# Revit family: Haworth_JiveTable_RacetrackLegs
name_source: partatom
category: Furniture Systems
revit_build: Autodesk Revit 2018 (Build: 20170223_1515(x64)
units: mm (PartAtom-declared; Revit-internal decimal feet)

## family parameters
Always vertical = Yes
Cut with Voids When Loaded = No
OmniClass Number = 23.40.70.14.64.21
OmniClass Title = Systems Furniture
Part Type = Normal
Room Calculation Point = No
Round Connector Dimension = Use Diameter
Shared = No
Work Plane-Based = No

## types (46) — shared parameters
Assembly Code = E2020200
Custom Size = No
Manufacturer = Haworth, Inc.
Max. Depth = 48"
Max. Height = 29"
Max. Width = 96"
Min. Depth = 30"
Min. Height = 16"
Min. Width = 48"
Model = Hawoth Jive
Revision Number = 0
Size = Verify Final Dim. w/ Haworth
Standard Depths = 30, 36, 42, 48 in.
Standard Height = 16, 20. 29 in.
Standard Widths = 48, 60, 72, 84, 96 in.
Table Thickness = 1 3/16"
URL = https://www.haworth.com
URL - Product = http://www.haworth.com
Warranty = http://www.haworth.com

## per-type parameters (varying)
| type | Actual Casters | Actual Depth | Actual Height | Actual Width | Casters | Depth | Description | Glides | Height | Leg Distance | Leg Height | Leg Length | Leg Spacing | Post Extruded Base | Post Round Base | T Leg Extruded | Table Radius | Width |
| 30d 48w 16h - Post Extruded Base - With Glides | No | 30" | 16" | 48" | No | 30" | Haworth Jive Table Racetrack Legs - 30d 48w 16h - Post Extruded Base - With Glides | Yes | 16" | 11 1/2" | 14 13/16" | 11" | 8" | Yes | No | No | 15" | 48" |
| 30d 60w 16h - Post Extruded Base - With Glides | No | 30" | 16" | 60" | No | 30" | Haworth Jive Table Racetrack Legs - 30d 60w 16h - Post Extruded Base - With Glides | Yes | 16" | 11 1/2" | 14 13/16" | 11" | 8" | Yes | No | No | 15" | 60" |
| 30d 72w 16h - Post Extruded Base - With Glides | No | 30" | 16" | 72" | No | 30" | Haworth Jive Table Racetrack Legs - 30d 72w 16h - Post Extruded Base - With Glides | Yes | 16" | 11 1/2" | 14 13/16" | 11" | 8" | Yes | No | No | 15" | 72" |
| 36d 60w 16h - Post Extruded Base - With Glides | No | 36" | 16" | 60" | No | 36" | Haworth Jive Table Racetrack Legs - 36d 60w 16h - Post Extruded Base - With Glides | Yes | 16" | 11 1/2" | 14 13/16" | 11" | 11" | Yes | No | No | 18" | 60" |
| 36d 72w 16h - Post Extruded Base - With Glides | No | 36" | 16" | 72" | No | 36" | Haworth Jive Table Racetrack Legs - 36d 72w 16h - Post Extruded Base - With Glides | Yes | 16" | 11 1/2" | 14 13/16" | 11" | 11" | Yes | No | No | 18" | 72" |
| 36d 84w 16h - Post Extruded Base - With Glides | No | 36" | 16" | 84" | No | 36" | Haworth Jive Table Racetrack Legs - 36d 84w 16h - Post Extruded Base - With Glides | Yes | 16" | 11 1/2" | 14 13/16" | 11" | 11" | Yes | No | No | 18" | 84" |
| 30d 48w 20h - Post Extruded Base - With Glides | No | 30" | 20" | 48" | No | 30" | Haworth Jive Table Racetrack Legs - 30d 48w 20h - Post Extruded Base - With Glides | Yes | 20" | 11 1/2" | 18 13/16" | 11" | 8" | Yes | No | No | 15" | 48" |
| 30d 60w 20h - Post Extruded Base - With Glides | No | 30" | 20" | 60" | No | 30" | Haworth Jive Table Racetrack Legs - 30d 60w 20h - Post Extruded Base - With Glides | Yes | 20" | 11 1/2" | 18 13/16" | 11" | 8" | Yes | No | No | 15" | 60" |
| 30d 72w 20h - Post Extruded Base - With Glides | No | 30" | 20" | 72" | No | 30" | Haworth Jive Table Racetrack Legs - 30d 72w 20h - Post Extruded Base - With Glides | Yes | 20" | 11 1/2" | 18 13/16" | 11" | 8" | Yes | No | No | 15" | 72" |
| 36d 60w 20h - Post Extruded Base - With Glides | No | 36" | 20" | 60" | No | 36" | Haworth Jive Table Racetrack Legs - 36d 60w 20h - Post Extruded Base - With Glides | Yes | 20" | 11 1/2" | 18 13/16" | 11" | 11" | Yes | No | No | 18" | 60" |
| 36d 72w 20h - Post Extruded Base - With Glides | No | 36" | 20" | 72" | No | 36" | Haworth Jive Table Racetrack Legs - 36d 72w 20h - Post Extruded Base - With Glides | Yes | 20" | 11 1/2" | 18 13/16" | 11" | 11" | Yes | No | No | 18" | 72" |
| 36d 84w 20h - Post Extruded Base - With Glides | No | 36" | 20" | 84" | No | 36" | Haworth Jive Table Racetrack Legs - 36d 84w 20h - Post Extruded Base - With Glides | Yes | 20" | 11 1/2" | 18 13/16" | 11" | 11" | Yes | No | No | 18" | 84" |
| 30d 48w 29h - Post Extruded Base - With Casters | Yes | 30" | 29" | 48" | Yes | 30" | Haworth Jive Table Racetrack Legs - 30d 48w 29h - Post Extruded Base - With Casters | No | 29" | 11 1/2" | 27 13/16" | 11" | 8" | Yes | No | No | 15" | 48" |
| 30d 60w 29h - Post Extruded Base - With Casters | Yes | 30" | 29" | 60" | Yes | 30" | Haworth Jive Table Racetrack Legs - 30d 60w 29h - Post Extruded Base - With Casters | No | 29" | 11 1/2" | 27 13/16" | 11" | 8" | Yes | No | No | 15" | 60" |
| 30d 72w 29h - Post Extruded Base - With Casters | Yes | 30" | 29" | 72" | Yes | 30" | Haworth Jive Table Racetrack Legs - 30d 72w 29h - Post Extruded Base - With Casters | No | 29" | 11 1/2" | 27 13/16" | 11" | 8" | Yes | No | No | 15" | 72" |
| 36d 60w 29h - Post Extruded Base - With Casters | Yes | 36" | 29" | 60" | Yes | 36" | Haworth Jive Table Racetrack Legs - 36d 60w 29h - Post Extruded Base - With Casters | No | 29" | 11 1/2" | 27 13/16" | 11" | 11" | Yes | No | No | 18" | 60" |
| 36d 72w 29h - Post Extruded Base - With Casters | Yes | 36" | 29" | 72" | Yes | 36" | Haworth Jive Table Racetrack Legs - 36d 72w 29h - Post Extruded Base - With Casters | No | 29" | 11 1/2" | 27 13/16" | 11" | 11" | Yes | No | No | 18" | 72" |
| 30d 48w 29h - Post Extruded Base - With Glides | No | 30" | 29" | 48" | No | 30" | Haworth Jive Table Racetrack Legs - 30d 48w 29h - Post Extruded Base - With Glides | Yes | 29" | 11 1/2" | 27 13/16" | 11" | 8" | Yes | No | No | 15" | 48" |
| 30d 60w 29h - Post Extruded Base - With Glides | No | 30" | 29" | 60" | No | 30" | Haworth Jive Table Racetrack Legs - 30d 60w 29h - Post Extruded Base - With Glides | Yes | 29" | 11 1/2" | 27 13/16" | 11" | 8" | Yes | No | No | 15" | 60" |
| 30d 72w 29h - Post Extruded Base - With Glides | No | 30" | 29" | 72" | No | 30" | Haworth Jive Table Racetrack Legs - 30d 72w 29h - Post Extruded Base - With Glides | Yes | 29" | 11 1/2" | 27 13/16" | 11" | 8" | Yes | No | No | 15" | 72" |
| 36d 60w 29h - Post Extruded Base - With Glides | No | 36" | 29" | 60" | No | 36" | Haworth Jive Table Racetrack Legs - 36d 60w 29h - Post Extruded Base - With Glides | Yes | 29" | 11 1/2" | 27 13/16" | 11" | 11" | Yes | No | No | 18" | 60" |
| 36d 72w 29h - Post Extruded Base - With Glides | No | 36" | 29" | 72" | No | 36" | Haworth Jive Table Racetrack Legs - 36d 72w 29h - Post Extruded Base - With Glides | Yes | 29" | 11 1/2" | 27 13/16" | 11" | 11" | Yes | No | No | 18" | 72" |
| 36d 84w 29h - Post Extruded Base - With Glides | No | 36" | 29" | 84" | No | 36" | Haworth Jive Table Racetrack Legs - 36d 84w 29h - Post Extruded Base - With Glides | Yes | 29" | 11 1/2" | 27 13/16" | 11" | 11" | Yes | No | No | 18" | 84" |
| 42d 84w 29h - Post Extruded Base - With Glides | No | 42" | 29" | 84" | No | 42" | Haworth Jive Table Racetrack Legs - 42d 84w 29h - Post Extruded Base - With Glides | Yes | 29" | 11 1/2" | 27 13/16" | 11" | 14" | Yes | No | No | 21" | 84" |
| 42d 96w 29h - Post Extruded Base - With Glides | No | 42" | 29" | 96" | No | 42" | Haworth Jive Table Racetrack Legs - 42d 96w 29h - Post Extruded Base - With Glides | Yes | 29" | 11 1/2" | 27 13/16" | 11" | 14" | Yes | No | No | 21" | 96" |
| 48d 96w 29h - Post Extruded Base - With Glides | No | 48" | 29" | 96" | No | 48" | Haworth Jive Table Racetrack Legs - 48d 96w 29h - Post Extruded Base - With Glides | Yes | 29" | 11 1/2" | 27 13/16" | 11" | 17" | Yes | No | No | 24" | 96" |
| 30d 48w 29h - Post Round Base - With Casters | Yes | 30" | 29" | 48" | Yes | 30" | Haworth Jive Table Racetrack Legs - 30d 48w 29h - Post Round Base - With Casters | No | 29" | 11 1/2" | 27 13/16" | 11" | 8" | No | Yes | No | 15" | 48" |
| 30d 60w 29h - Post Round Base - With Casters | Yes | 30" | 29" | 60" | Yes | 30" | Haworth Jive Table Racetrack Legs - 30d 60w 29h - Post Round Base - With Casters | No | 29" | 11 1/2" | 27 13/16" | 11" | 8" | No | Yes | No | 15" | 60" |
| 30d 72w 29h - Post Round Base - With Casters | Yes | 30" | 29" | 72" | Yes | 30" | Haworth Jive Table Racetrack Legs - 30d 72w 29h - Post Round Base - With Casters | No | 29" | 11 1/2" | 27 13/16" | 11" | 8" | No | Yes | No | 15" | 72" |
| 36d 60w 29h - Post Round Base - With Casters | Yes | 36" | 29" | 60" | Yes | 36" | Haworth Jive Table Racetrack Legs - 36d 60w 29h - Post Round Base - With Casters | No | 29" | 11 1/2" | 27 13/16" | 11" | 11" | No | Yes | No | 18" | 60" |
| 36d 72w 29h - Post Round Base - With Casters | Yes | 36" | 29" | 72" | Yes | 36" | Haworth Jive Table Racetrack Legs - 36d 72w 29h - Post Round Base - With Casters | No | 29" | 11 1/2" | 27 13/16" | 11" | 11" | No | Yes | No | 18" | 72" |
| 30d 48w 29h - Post Round Base - With Glides | No | 30" | 29" | 48" | No | 30" | Haworth Jive Table Racetrack Legs - 30d 48w 29h - Post Round Base - With Glides | Yes | 29" | 11 1/2" | 27 13/16" | 11" | 8" | No | Yes | No | 15" | 48" |
| 30d 60w 29h - Post Round Base - With Glides | No | 30" | 29" | 60" | No | 30" | Haworth Jive Table Racetrack Legs - 30d 60w 29h - Post Round Base - With Glides | Yes | 29" | 11 1/2" | 27 13/16" | 11" | 8" | No | Yes | No | 15" | 60" |
| 30d 72w 29h - Post Round Base - With Glides | No | 30" | 29" | 72" | No | 30" | Haworth Jive Table Racetrack Legs - 30d 72w 29h - Post Round Base - With Glides | Yes | 29" | 11 1/2" | 27 13/16" | 11" | 8" | No | Yes | No | 15" | 72" |
| 36d 60w 29h - Post Round Base - With Glides | No | 36" | 29" | 60" | No | 36" | Haworth Jive Table Racetrack Legs - 36d 60w 29h - Post Round Base - With Glides | Yes | 29" | 11 1/2" | 27 13/16" | 11" | 11" | No | Yes | No | 18" | 60" |
| 36d 72w 29h - Post Round Base - With Glides | No | 36" | 29" | 72" | No | 36" | Haworth Jive Table Racetrack Legs - 36d 72w 29h - Post Round Base - With Glides | Yes | 29" | 11 1/2" | 27 13/16" | 11" | 11" | No | Yes | No | 18" | 72" |
| 30d 48w 29h - T Leg Extruded - With Casters | Yes | 30" | 29" | 48" | Yes | 30" | Haworth Jive Table Racetrack Legs - 30d 48w 29h - T Leg Extruded - With Casters | No | 29" | 11 205/256" | 27 13/16" | 11" | 8" | No | No | Yes | 15" | 48" |
| 30d 60w 29h - T Leg Extruded - With Casters | Yes | 30" | 29" | 60" | Yes | 30" | Haworth Jive Table Racetrack Legs - 30d 60w 29h - T Leg Extruded - With Casters | No | 29" | 11 205/256" | 27 13/16" | 11" | 8" | No | No | Yes | 15" | 60" |
| 30d 72w 29h - T Leg Extruded - With Casters | Yes | 30" | 29" | 72" | Yes | 30" | Haworth Jive Table Racetrack Legs - 30d 72w 29h - T Leg Extruded - With Casters | No | 29" | 11 205/256" | 27 13/16" | 11" | 8" | No | No | Yes | 15" | 72" |
| 36d 60w 29h - T Leg Extruded - With Casters | Yes | 36" | 29" | 60" | Yes | 36" | Haworth Jive Table Racetrack Legs - 36d 60w 29h - T Leg Extruded - With Casters | No | 29" | 13 205/256" | 27 13/16" | 13" | 11" | No | No | Yes | 18" | 60" |
| 36d 72w 29h - T Leg Extruded - With Casters | Yes | 36" | 29" | 72" | Yes | 36" | Haworth Jive Table Racetrack Legs - 36d 72w 29h - T Leg Extruded - With Casters | No | 29" | 13 205/256" | 27 13/16" | 13" | 11" | No | No | Yes | 18" | 72" |
| 30d 48w 29h - T Leg Extruded - With Glides | No | 30" | 29" | 48" | No | 30" | Haworth Jive Table Racetrack Legs - 30d 48w 29h - T Leg Extruded - With Glides | Yes | 29" | 11 205/256" | 27 13/16" | 11" | 8" | No | No | Yes | 15" | 48" |
| 30d 60w 29h - T Leg Extruded - With Glides | No | 30" | 29" | 60" | No | 30" | Haworth Jive Table Racetrack Legs - 30d 60w 29h - T Leg Extruded - With Glides | Yes | 29" | 11 205/256" | 27 13/16" | 11" | 8" | No | No | Yes | 15" | 60" |
| 30d 72w 29h - T Leg Extruded - With Glides | No | 30" | 29" | 72" | No | 30" | Haworth Jive Table Racetrack Legs - 30d 72w 29h - T Leg Extruded - With Glides | Yes | 29" | 11 205/256" | 27 13/16" | 11" | 8" | No | No | Yes | 15" | 72" |
| 36d 60w 29h - T Leg Extruded - With Glides | No | 36" | 29" | 60" | No | 36" | Haworth Jive Table Racetrack Legs - 36d 60w 29h - T Leg Extruded - With Glides | Yes | 29" | 13 205/256" | 27 13/16" | 13" | 11" | No | No | Yes | 18" | 60" |
| 36d 72w 29h - T Leg Extruded - With Glides | No | 36" | 29" | 72" | No | 36" | Haworth Jive Table Racetrack Legs - 36d 72w 29h - T Leg Extruded - With Glides | Yes | 29" | 13 205/256" | 27 13/16" | 13" | 11" | No | No | Yes | 18" | 72" |

## geometry (parser evidence)
native form markers: Sweep x31
no freeform markers — native parametric forms only
